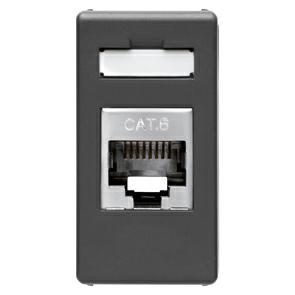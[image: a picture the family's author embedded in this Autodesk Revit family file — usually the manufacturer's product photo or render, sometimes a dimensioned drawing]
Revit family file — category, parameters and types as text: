
# Revit family: Domotics-DomesticRanges-GEWISS-SYSTEM_DATA-SOCKET-OUTLET_RJ45
name_source: partatom
category: Apparecchi elettrici
revit_build: Autodesk Revit 2016 (Build: 20161004_0715(x64)
units: mm (PartAtom-declared; Revit-internal decimal feet)

## family parameters
Condiviso = Sì
Host = Superficie
Mantenere orientamento annotazione = Sì
Numero OmniClass = 23.80.50.14
Punto di calcolo locali = Sì
Quota connettore circolare = Usa diametro
Taglio con vuoti quando caricato = Sì
Tipo di parte = Normale
Titolo OmniClass = Plug Connectors

## types (10) — shared parameters
Carico apparente = 0 VA
Catalogue = DOMOTICS
Connection = Toolless
Connection type = Insulation puncture
Description: = RJ45
Electrocod = 3722
IDF = e377b961-ed39-430b-951e-6a8c3b17b373
IDT = 4cc29fa8-c327-42cf-aab6-241808a3342b
Immagine tipo = GW21686.jpg
Larghezza presa = 23 mm  [stored 0.0754593 ft]
N. poli = 1
No. SYSTEM modules = 1
No. pairs = 4
Produttore = GEWISS S.p.A.
Prospetto di default = 1219 mm
SEO = Socket outlet
Simbolo = SIMBOLO PRESE TELEFONO : PRESA TEL
Technical sheet = https://www.gewiss.com
Tipo_ = SYSTEM PRESE RJ45_BASE : GW21686 - Nero - 6 FTP
URL = https://www.gewiss.com
Version file RFA = 19.4
Volt = 0 V

## per-type parameters (varying)
| type | Cables | Catalogue Range | Colour | Compatibility | Description. | Descrizione | EAN code | Modello | Use category |
| GW20243 - Phone s.-outlet RJ45 cat.5e white | FTP | SYSTEM WHITE | White |  | RJ45 | PHONE S.-OUTLET RJ45 CAT.5E SY/WT | 8011564038509 | GW20243 | 5e |
| GW20684 - Socket-outlet RJ45 cat6 utp white | UTP | SYSTEM WHITE | White |  | RJ45 | SOCKET-OUTLET RJ45 CAT6 UTP SY/WT | 8011564117655 | GW20684 | 6 |
| GW20271 - Data connector RJ45 cat.5e utp white | UTP | SYSTEM WHITE | White | AMP / Keystone Jack | RJ45 connector | DATA CONNECTOR RJ45 CAT.5E UTP SY/WT | 8011564045828 | GW20271 | 5e |
| GW21684 - Socket-outlet RJ45 cat6 utp black | UTP | SYSTEM BLACK | Black |  | RJ45 connector | SOCKET-OUTLET RJ45 CAT6 UTP SY/BK | 8011564128873 | GW21684 | 6 |
| GW21243 - Phone s.-outlet RJ45 cat.5e black | FTP | SYSTEM BLACK | Black |  | RJ45 connector | PHONE S.-OUTLET RJ45 CAT.5E SY/BK | 8011564128941 | GW21243 | 5e |
| GW21271 - Data connector RJ45 cat.5e utp black | UTP | SYSTEM BLACK | Black | AMP / Keystone Jack | RJ45 | DATA CONNECTOR RJ45 CAT.5E UTP SY/BK | 8011564128934 | GW21271 | 5e |
| GW21686 - Socket-outlet RJ45 cat6 ftp black | FTP | SYSTEM BLACK | Black |  | RJ45 connector | SOCKET-OUTLET RJ45 CAT6 FTP SY/BK | 8011564247307 | GW21686 | 6 |
| GW21685 - Socket-outlet RJ45 cat6 utp black | UTP | SYSTEM BLACK | Black |  | RJ45 connector | SOCKET-OUTLET RJ45 CAT6 UTP SY/BK | 8011564247291 | GW21685 | 6 |
| GW20685 - Socket-outlet RJ45 cat6 utp white | UTP | SYSTEM WHITE | White |  | RJ45 connector | SOCKET-OUTLET RJ45 CAT6 UTP SY/WT | 8011564247277 | GW20685 | 6 |
| GW20686 - Socket-outlet RJ45 cat6 ftp white | FTP | SYSTEM WHITE | White |  | RJ45 connector | SOCKET-OUTLET RJ45 CAT6 FTP SY/WT | 8011564247284 | GW20686 | 6 |

note: [stored X ft] marks values corroborated as IEEE doubles in the binary element streams (Revit-internal decimal feet)

## geometry (parser evidence)
native form markers: Sweep x1
no freeform markers — native parametric forms only
